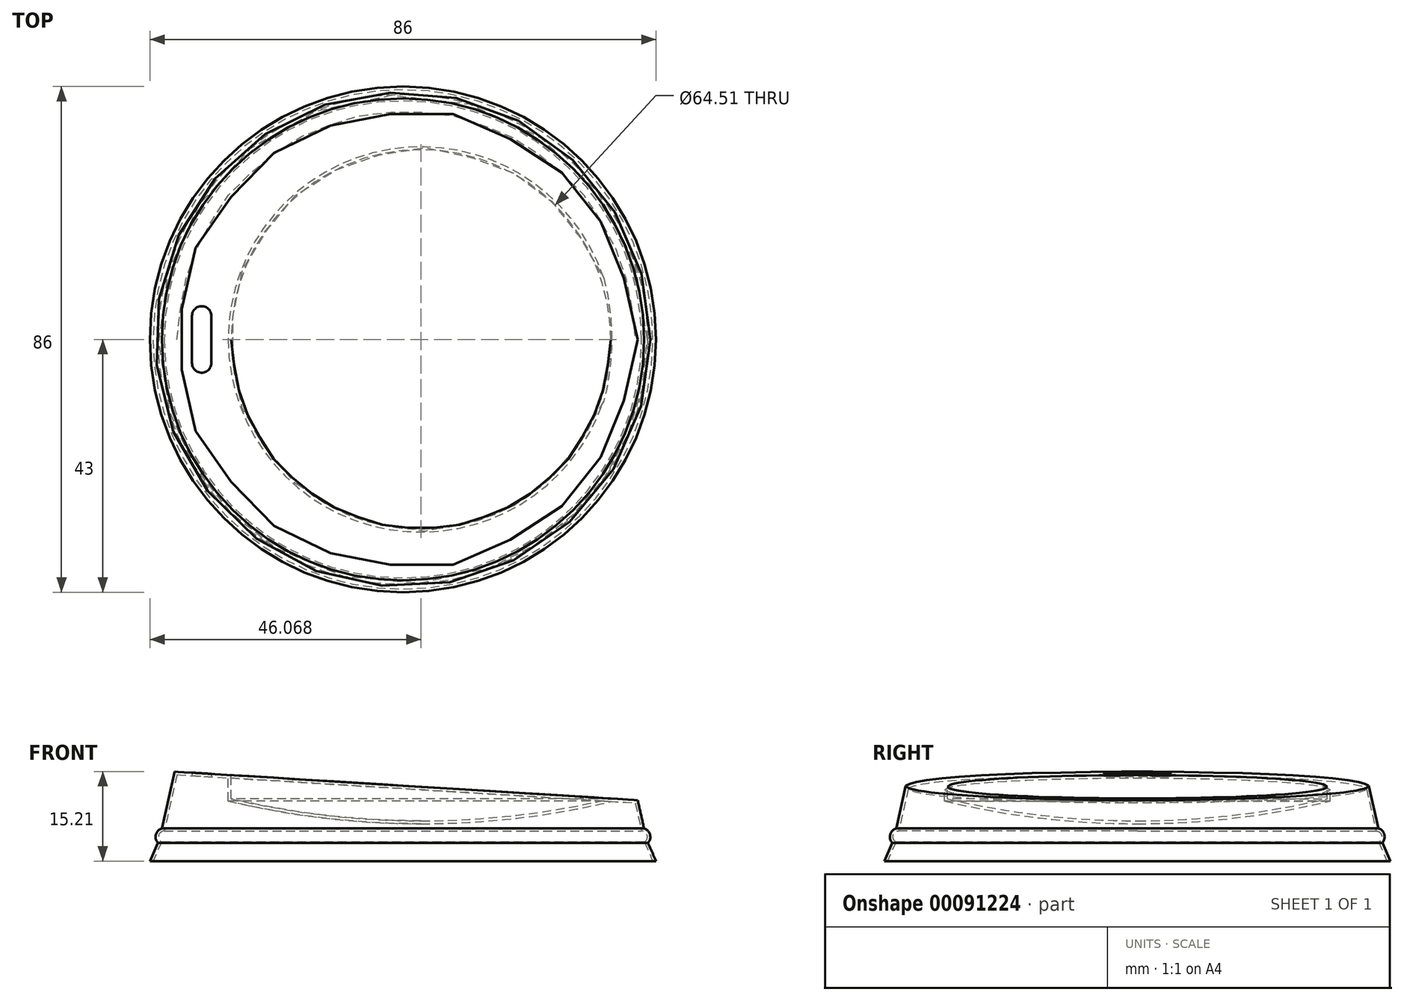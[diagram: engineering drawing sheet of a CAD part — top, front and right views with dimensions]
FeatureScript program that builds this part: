
annotation { "Feature Type Name" : "Feature", "Feature Type Description" : "" }
export const myFeature = defineFeature(function(context is Context, id is Id, definition is map)
    precondition{}
    {
        {
            var Q0;
            Q0=qCreatedBy(makeId("Front.planeOp"),FACE);
            var sketch = newSketch(context, id + "F0", { "sketchPlane" : qUnion([Q0])});
            skLineSegment(sketch, "E0", {"start": v(0, 0) * mm, "end": v(43, 0) * mm});
            skLineSegment(sketch, "E1", {"start": v(43, 0) * mm, "end": v(41.64, 3.1) * mm});
            skLineSegment(sketch, "E2", {"start": v(40.97, 5.56) * mm, "end": v(38.61, 15.97) * mm});
            skLineSegment(sketch, "E3", {"start": v(38.61, 15.97) * mm, "end": v(0, 15.97) * mm});
            skLineSegment(sketch, "E4", {"start": v(0, 15.97) * mm, "end": v(0, 0) * mm});
            skArc(sketch, "E5", {"start": v(41.64, 3.1) * mm, "mid": v(41.98, 4.52) * mm, "end": v(40.97, 5.56) * mm});
            skSolve(sketch);
        }
        {
            var Q0;
            Q0=makeQuery(id+"F0.imprint","IMPRINT",FACE,{"disambiguationData":[TD([[makeQuery(id+"F0.imprint","IMPRINT",EDGE,{"derivedFrom":sQuery(id+"F0.wireOp",EDGE,"E0")}),1.0]])]});
            var Q1;
            Q1=sQuery(id+"F0.wireOp",EDGE,"E4");
            revolve(context, id + "F1", {"entities" : qUnion([Q0]), "axis" : qUnion([Q1]), "revolveType" : RevolveType.FULL});
        }
        {
            var Q0;
            Q0=qCreatedBy(makeId("Front.planeOp"),FACE);
            var sketch = newSketch(context, id + "F2", { "sketchPlane" : qUnion([Q0])});
            skLineSegment(sketch, "E6", {"start": v(3.07, 6.84) * mm, "end": v(3.07, 17.01) * mm, "construction": true});
            skLineSegment(sketch, "E7", {"start": v(3.07, 17.01) * mm, "end": v(35.32, 17.01) * mm});
            skArc(sketch, "E8", {"start": v(3.07, 6.84) * mm, "mid": v(19.3, 7.79) * mm, "end": v(35.32, 10.6) * mm});
            skLineSegment(sketch, "E9", {"start": v(35.32, 17.01) * mm, "end": v(35.32, 10.6) * mm});
            skLineSegment(sketch, "E10", {"start": v(3.07, 17.01) * mm, "end": v(3.07, 6.84) * mm});
            skSolve(sketch);
        }
        {
            var Q0;
            Q0=makeQuery(id+"F2.imprint","IMPRINT",FACE,{"disambiguationData":[TD([[makeQuery(id+"F2.imprint","IMPRINT",EDGE,{"derivedFrom":sQuery(id+"F2.wireOp",EDGE,"E7")}),-1.0]])]});
            var Q1;
            Q1=sQuery(id+"F2.wireOp",EDGE,"E6");
            revolve(context, id + "F3", {"operationType" : NewBodyOperationType.REMOVE, "entities" : qUnion([Q0]), "axis" : qUnion([Q1]), "revolveType" : RevolveType.FULL, "oppositeDirection" : true});
        }
        {
            var Q0;
            Q0=qCreatedBy(makeId("Front.planeOp"),FACE);
            var sketch = newSketch(context, id + "F4", { "sketchPlane" : qUnion([Q0])});
            skLineSegment(sketch, "E11", {"start": v(-41.17, 15.36) * mm, "end": v(53.02, 9.55) * mm});
            skLineSegment(sketch, "E12", {"start": v(53.02, 9.55) * mm, "end": v(53.02, 21.17) * mm});
            skLineSegment(sketch, "E13", {"start": v(53.02, 21.17) * mm, "end": v(-41.17, 21.17) * mm});
            skLineSegment(sketch, "E14", {"start": v(-41.17, 21.17) * mm, "end": v(-41.17, 15.36) * mm});
            skSolve(sketch);
        }
        {
            var Q0;
            Q0 = qSketchRegion(id + "F4", true);
            extrude(context, id + "F5", {"entities" : qUnion([Q0]), "operationType" : NewBodyOperationType.REMOVE, "endBound" : BoundingType.THROUGH_ALL, "oppositeDirection" : true, "depth" : 25 * mm});
        }
        {
            var Q0;
            Q0 = qSketchRegion(id + "F4", true);
            extrude(context, id + "F6", {"entities" : qUnion([Q0]), "operationType" : NewBodyOperationType.REMOVE, "endBound" : BoundingType.THROUGH_ALL, "depth" : 25 * mm});
        }
        {
            var Q0;
            Q0=qCreatedBy(makeId("Top.planeOp"),FACE);
            var sketch = newSketch(context, id + "F7", { "sketchPlane" : qUnion([Q0])});
            skLineSegment(sketch, "E15", {"start": v(-32.53, 4) * mm, "end": v(-32.53, -4) * mm});
            skLineSegment(sketch, "E16", {"start": v(-35.85, 4) * mm, "end": v(-35.85, -4) * mm});
            skArc(sketch, "E17", {"start": v(-32.53, -4) * mm, "mid": v(-34.2, -5.66) * mm, "end": v(-35.85, -4) * mm});
            skArc(sketch, "E18", {"start": v(-32.53, 4) * mm, "mid": v(-34.2, 5.66) * mm, "end": v(-35.85, 4) * mm});
            skSolve(sketch);
        }
        {
            var Q0;
            Q0=makeQuery(id+"F1.opRevolve","SWEPT_FACE",FACE,{"disambiguationData":[OSD([sQuery(id+"F0.wireOp",EDGE,"E0")])]});
            shell(context, id + "F8", {"entities" : qUnion([Q0]), "thickness" : 0.5 * mm});
        }
        {
            var Q0;
            Q0 = qSketchRegion(id + "F7", true);
            extrude(context, id + "F9", {"entities" : qUnion([Q0]), "operationType" : NewBodyOperationType.REMOVE, "depth" : 25 * mm});
        }
    });
